# Revit family: Casement_36_E_Side_Hung_Custom
name_source: partatom
category: Windows
revit_build: Autodesk Revit 2014 (Build: 20130308_1515(x64)
units: mm (PartAtom-declared; Revit-internal decimal feet)

## types (1)
- 36-TypeE-SideHung-Custom
    Aluminium Thickness = 1 mm  [stored 0.00328084 ft]
    Area Pane Left Bottom = 0.14 m²
    Area Pane Left Top = 0.52 m²
    Area Pane Right = 0.37 m²
    Bead SG Gap = 13 mm  [stored 0.0426509 ft]
    Casement Dimension = 36 mm  [stored 0.11811 ft]
    Custom Sash Height = 1154 mm  [stored 3.78609 ft]
    Custom Sash Width = 554 mm  [stored 1.81759 ft]
    Custom Windload = 1000 mm  [stored 3.28084 ft]
    Custom Window Exterior Offset = 82 mm  [stored 0.269029 ft]
    Custom Window Height = 1500 mm  [stored 4.92126 ft]
    Custom Window Width = 900 mm  [stored 2.95276 ft]
    DG Extrusion Start = 8 mm  [stored 0.0262467 ft]
    DG Gasket Finish = Double Glazing Gasket Material
    DG Thickness Calc = 4 mm  [stored 0.0131234 ft]
    Default Sill Height = 800 mm  [stored 2.62467 ft]
    Depth Bead = 22 mm  [stored 0.0721785 ft]
    Depth Mullion = 37 mm  [stored 0.121391 ft]
    Description = Window 36mm, Type E side hung custom
    Frame Center Offset = 18 mm  [stored 0.0590551 ft]
    Height = 1500 mm  [stored 4.92126 ft]
    Height Fixed Pane Bottom LHS = 270 mm  [stored 0.885827 ft]
    Height Fixed Pane RHS = 1440 mm  [stored 4.72441 ft]
    Height Panel 1 = 1139 mm  [stored 3.73688 ft]
    Height Sash = 1124 mm  [stored 3.68766 ft]
    Height Sash Opening = 1154 mm  [stored 3.78609 ft]
    Length Mullion = 1500 mm  [stored 4.92126 ft]
    Length Transom = 540 mm  [stored 1.77165 ft]
    Limit Fixed Pane Height Max = 1800 mm  [stored 5.90551 ft]
    Limit Fixed Pane Height Min = 200 mm  [stored 0.656168 ft]
    Limit Fixed Pane Width Max = 1500 mm  [stored 4.92126 ft]
    Limit Fixed Pane Width Min = 200 mm  [stored 0.656168 ft]
    Limit Sash Height Max = 1300 mm  [stored 4.26509 ft]
    Limit Sash Height Min = 300 mm  [stored 0.984252 ft]
    Limit Sash Width Max = 600 mm  [stored 1.9685 ft]
    Limit Sash Width Min = 300 mm  [stored 0.984252 ft]
    Limit Window Height Max = 1860 mm  [stored 6.10236 ft]
    Limit Window Height Min = 1430 mm  [stored 4.6916 ft]
    Limit Window Width Max = 2130 mm  [stored 6.98819 ft]
    Limit Window Width Min = 830 mm  [stored 2.7231 ft]
    Manufacturer = Crealco
    Max Pane Area = 0.52 m²
    Max System DG One Piece Thickness = 6 mm  [stored 0.019685 ft]
    Max System DG Unit Thickness = 25 mm  [stored 0.082021 ft]
    Model = Casement 36
    Mullion Depth Windload Based = 37 mm  [stored 0.121391 ft]
    Offset Bead SG Center Reversed = 18 mm  [stored 0.0590551 ft]
    Offset Mullion Left = 570 mm  [stored 1.87008 ft]
    Offset Panel 3 Bead Top = 1200 mm
    Offset Panel 4 Left = 600 mm  [stored 1.9685 ft]
    Offset Sash Left = 23 mm  [stored 0.0754593 ft]
    Offset Sash Top = 23 mm  [stored 0.0754593 ft]
    Offset Transom Top = 1170 mm
    Offset Window Exterior = 100 mm  [stored 0.328084 ft]
    SG Gasket Thickness = 6 mm  [stored 0.019685 ft]
    Sash Center Offset = 15 mm  [stored 0.0492126 ft]
    Sash Overlap = 7 mm  [stored 0.0229659 ft]
    Sash Spacing Inner = 8 mm  [stored 0.0262467 ft]
    URL = http://www.crealco.co.za
    Wall Closure = By host
    Width = 900 mm  [stored 2.95276 ft]
    Width Bead = 15 mm  [stored 0.0492126 ft]
    Width Fixed Pane Bottom LHS = 540 mm  [stored 1.77165 ft]
    Width Fixed Pane RHS = 270 mm  [stored 0.885827 ft]
    Width Panel 1 = 540 mm  [stored 1.77165 ft]
    Width Profile = 30 mm  [stored 0.0984252 ft]
    Width Sash = 524 mm  [stored 1.71916 ft]
    Width Sash Opening = 554 mm  [stored 1.81759 ft]
    Windload Design = 1000 mm  [stored 3.28084 ft]

note: [stored X ft] marks values corroborated as IEEE doubles in the binary element streams (Revit-internal decimal feet)

## geometry (parser evidence)
native form markers: Blend x4, Extrusion x1, Sweep x24
no freeform markers — native parametric forms only
